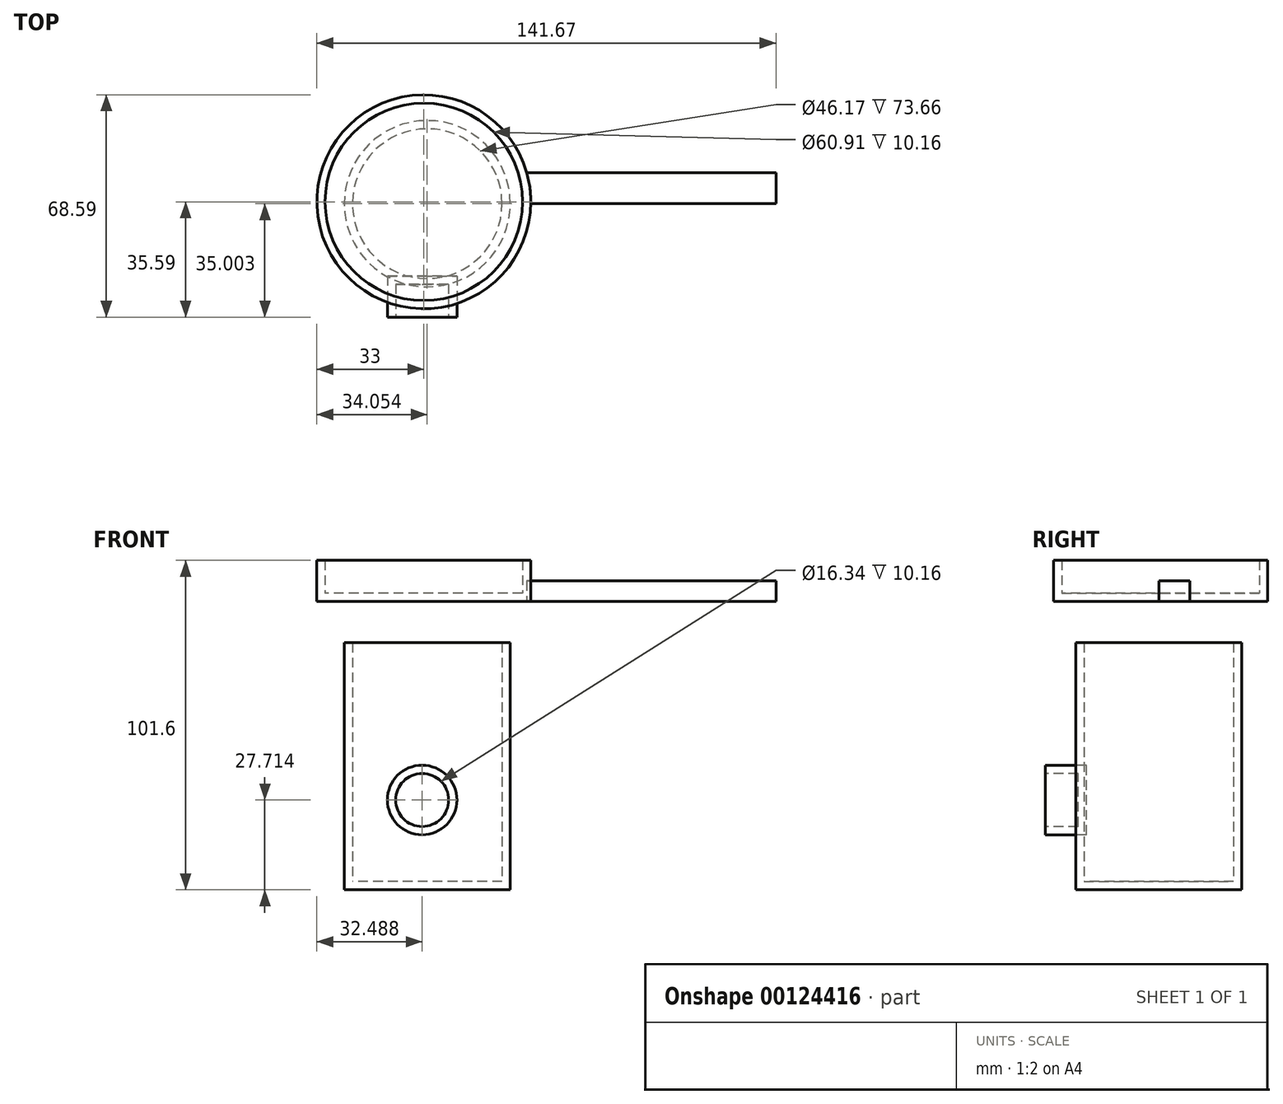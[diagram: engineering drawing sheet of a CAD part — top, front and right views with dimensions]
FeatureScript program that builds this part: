
annotation { "Feature Type Name" : "Feature", "Feature Type Description" : "" }
export const myFeature = defineFeature(function(context is Context, id is Id, definition is map)
    precondition{}
    {
        {
            var Q0;
            Q0=qCreatedBy(makeId("Top.planeOp"),FACE);
            var sketch = newSketch(context, id + "F0", { "sketchPlane" : qUnion([Q0])});
            skCircle(sketch, "E0", {"center": v(-35.86, 28.65) * mm, "radius": 25.63 * mm});
            skSolve(sketch);
        }
        {
            var Q0;
            Q0 = qSketchRegion(id + "F0", true);
            extrude(context, id + "F1", {"entities" : qUnion([Q0]), "depth" : 76.2 * mm});
        }
        {
            var Q0;
            Q0=makeQuery(id+"F1.opExtrude","CAP_FACE",FACE,{"disambiguationData":[OSD([sQuery(id+"F0.wireOp",EDGE,"E0")])],"isStart":false});
            shell(context, id + "F2", {"entities" : qUnion([Q0]), "thickness" : 2.54 * mm});
        }
        {
            var Q0;
            Q0=qCreatedBy(makeId("Front.planeOp"),FACE);
            cPlane(context, id + "F3", {"entities" : qUnion([Q0]), "cplaneType" : CPlaneType.OFFSET, "offset" : 6.35 * mm, "width" : 152.4 * mm, "height" : 152.4 * mm});
        }
        {
            var Q0;
            Q0=qCreatedBy(id+"F3.planeOp",FACE);
            var sketch = newSketch(context, id + "F4", { "sketchPlane" : qUnion([Q0])});
            skCircle(sketch, "E1", {"center": v(-37.42, 27.71) * mm, "radius": 10.71 * mm});
            skSolve(sketch);
        }
        {
            var Q0;
            Q0 = qSketchRegion(id + "F4", true);
            extrude(context, id + "F5", {"entities" : qUnion([Q0]), "oppositeDirection" : true, "depth" : 12.7 * mm});
        }
        {
            var Q0;
            Q0=makeQuery(id+"F5.opExtrude","CAP_FACE",FACE,{"disambiguationData":[OSD([sQuery(id+"F4.wireOp",EDGE,"E1")])],"isStart":true});
            shell(context, id + "F6", {"entities" : qUnion([Q0]), "thickness" : 2.54 * mm});
        }
        {
            var Q0;
            Q0=qCreatedBy(makeId("Front.planeOp"),FACE);
            cPlane(context, id + "F7", {"entities" : qUnion([Q0]), "cplaneType" : CPlaneType.OFFSET, "offset" : 38.1 * mm, "oppositeDirection" : true, "width" : 152.4 * mm, "height" : 152.4 * mm});
        }
        {
            var Q0;
            Q0=qCreatedBy(makeId("Right.planeOp"),FACE);
            cPlane(context, id + "F8", {"entities" : qUnion([Q0]), "cplaneType" : CPlaneType.OFFSET, "offset" : 63.5 * mm, "oppositeDirection" : true, "width" : 152.4 * mm, "height" : 152.4 * mm});
        }
        {
            var Q0;
            Q0=qCreatedBy(makeId("Top.planeOp"),FACE);
            cPlane(context, id + "F9", {"entities" : qUnion([Q0]), "cplaneType" : CPlaneType.OFFSET, "offset" : 88.9 * mm, "width" : 152.4 * mm, "height" : 152.4 * mm});
        }
        {
            var Q0;
            Q0=qCreatedBy(id+"F9.planeOp",FACE);
            var sketch = newSketch(context, id + "F10", { "sketchPlane" : qUnion([Q0])});
            skCircle(sketch, "E2", {"center": v(-36.91, 29.24) * mm, "radius": 33 * mm});
            skSolve(sketch);
        }
        {
            var Q0;
            Q0 = qSketchRegion(id + "F10", true);
            extrude(context, id + "F11", {"entities" : qUnion([Q0]), "depth" : 12.7 * mm});
        }
        {
            var Q0;
            Q0=makeQuery(id+"F11.opExtrude","CAP_FACE",FACE,{"disambiguationData":[OSD([sQuery(id+"F10.wireOp",EDGE,"E2")])],"isStart":false});
            shell(context, id + "F12", {"entities" : qUnion([Q0]), "thickness" : 2.54 * mm});
        }
        {
            var Q0;
            Q0=qCreatedBy(id+"F9.planeOp",FACE);
            var sketch = newSketch(context, id + "F13", { "sketchPlane" : qUnion([Q0])});
            skLineSegment(sketch, "E3", {"start": v(-5.64, 38.23) * mm, "end": v(71.76, 38.23) * mm});
            skLineSegment(sketch, "E4", {"start": v(71.76, 38.23) * mm, "end": v(71.76, 28.68) * mm});
            skLineSegment(sketch, "E5", {"start": v(71.76, 28.68) * mm, "end": v(-5.64, 28.68) * mm});
            skLineSegment(sketch, "E6", {"start": v(-5.64, 38.23) * mm, "end": v(-5.64, 28.68) * mm});
            skSolve(sketch);
        }
        {
            var Q0;
            Q0 = qSketchRegion(id + "F13", true);
            extrude(context, id + "F14", {"entities" : qUnion([Q0]), "operationType" : NewBodyOperationType.ADD, "depth" : 6.35 * mm});
        }
    });
